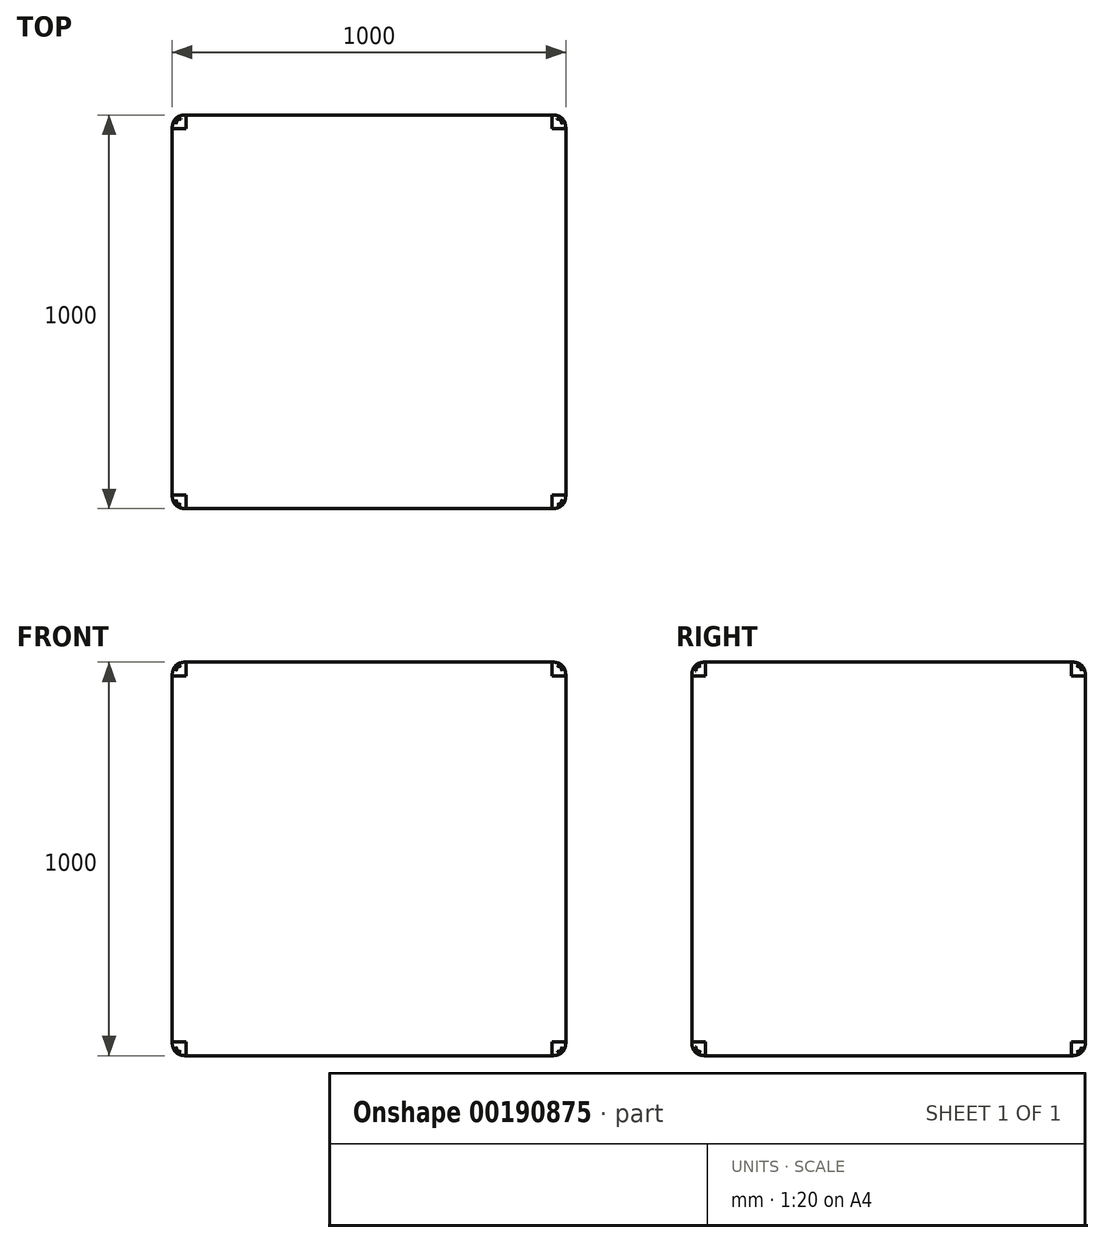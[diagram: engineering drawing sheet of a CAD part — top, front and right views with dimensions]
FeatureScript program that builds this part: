
annotation { "Feature Type Name" : "Feature", "Feature Type Description" : "" }
export const myFeature = defineFeature(function(context is Context, id is Id, definition is map)
    precondition{}
    {
        {
            var Q0;
            Q0=qCreatedBy(makeId("Front.planeOp"),FACE);
            var sketch = newSketch(context, id + "F0", { "sketchPlane" : qUnion([Q0])});
            skLineSegment(sketch, "E0.bottom", {"start": v(500, 500) * mm, "end": v(-500, 500) * mm});
            skLineSegment(sketch, "E0.top", {"start": v(500, -500) * mm, "end": v(-500, -500) * mm});
            skLineSegment(sketch, "E0.left", {"start": v(500, 500) * mm, "end": v(500, -500) * mm});
            skLineSegment(sketch, "E0.right", {"start": v(-500, 500) * mm, "end": v(-500, -500) * mm});
            skPoint(sketch, "E0.middle", {"position": v(0, 0) * mm});
            skSolve(sketch);
        }
        {
            var Q0;
            Q0 = qSketchRegion(id + "F0", true);
            extrude(context, id + "F1", {"entities" : qUnion([Q0]), "depth" : 1000 * mm, "symmetric" : true});
        }
        {
            var Q0;
            Q0=makeQuery(id+"F1.opExtrude","SWEPT_FACE",FACE,{"disambiguationData":[OSD([sQuery(id+"F0.wireOp",EDGE,"E0.bottom")])]});
            var Q1;
            Q1=makeQuery(id+"F1.opExtrude","SWEPT_FACE",FACE,{"disambiguationData":[OSD([sQuery(id+"F0.wireOp",EDGE,"E0.top")])]});
            var Q2;
            Q2=makeQuery(id+"F1.opExtrude","SWEPT_FACE",FACE,{"disambiguationData":[OSD([sQuery(id+"F0.wireOp",EDGE,"E0.left")])]});
            var Q3;
            Q3=makeQuery(id+"F1.opExtrude","SWEPT_FACE",FACE,{"disambiguationData":[OSD([sQuery(id+"F0.wireOp",EDGE,"E0.right")])]});
            fillet(context, id + "F2", {"entities" : qUnion([Q0, Q1, Q2, Q3]), "radius" : 35 * mm, "tangentPropagation" : true, "rho" : 0.5, "crossSection" : FilletCrossSection.CONIC, "allowEdgeOverflow" : false});
        }
    });
